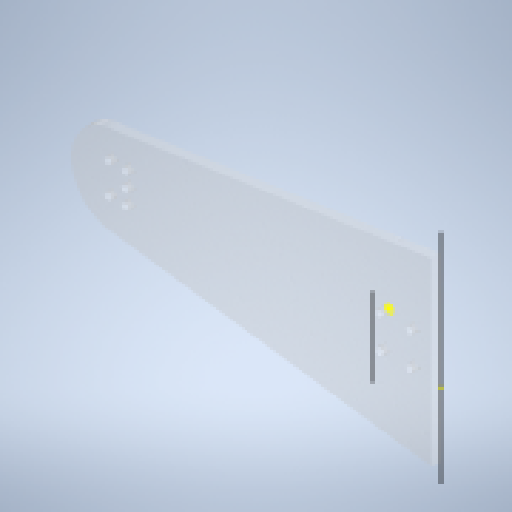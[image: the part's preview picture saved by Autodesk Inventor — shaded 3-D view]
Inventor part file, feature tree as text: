
AUTODESK INVENTOR PART (.ipt)
format: ipt  version: 2023.1 (Build 271208000, 208)  size: 183,808 bytes
history: native  units: in
note: dims shown in document units (in); Inventor stores cm internally (conversion verified against a paired STEP export)
features: reference x10, other x4, extrude x1, hole x1, sketch x1
ambient origin geometry x8: Origin, YZ Plane, XZ Plane, XY Plane, X Axis, Y Axis, Z Axis, Center Point
bodies: Solid1 (feature_tree)
feature tree (17):
  extrude  "Extrusion1"  Depth=0.0787in
  hole  "Hole1"  [1 undecoded]
  reference  "Reference2"
  reference  "Reference3"
  reference  "Reference4"
  reference  "Reference5"
  reference  "Reference6"
  reference  "Reference7"
  reference  "Reference8"
  reference  "Reference9"
  reference  "Reference10"
  reference  "Reference11"
  sketch  "Sketch2"  dims[d0=3.937in d1=1.9685in d2=1.9685in d3=6.8898in d4=0.1969in d5=0.0in d7=0.1339in d8=0.1181in d9=0.0in d10=0.1181in d11=1.4409in d12=0.8504in d14=0.1181in d15=0.2362in d16=0.1575in d17=0.0787in d18=90.0deg d19=0.315in d20=0.8108in]
  other  "Ensamble.iam"
  other  "base:1"
  other  "SoporteEncoder:1"
  other  "SoporteUnion:1"
note: 1 required parameter value undecoded (feature->parameter linkage not recoverable at this tier; creation-order binding heuristic only, values carry confidence <= 0.55)
